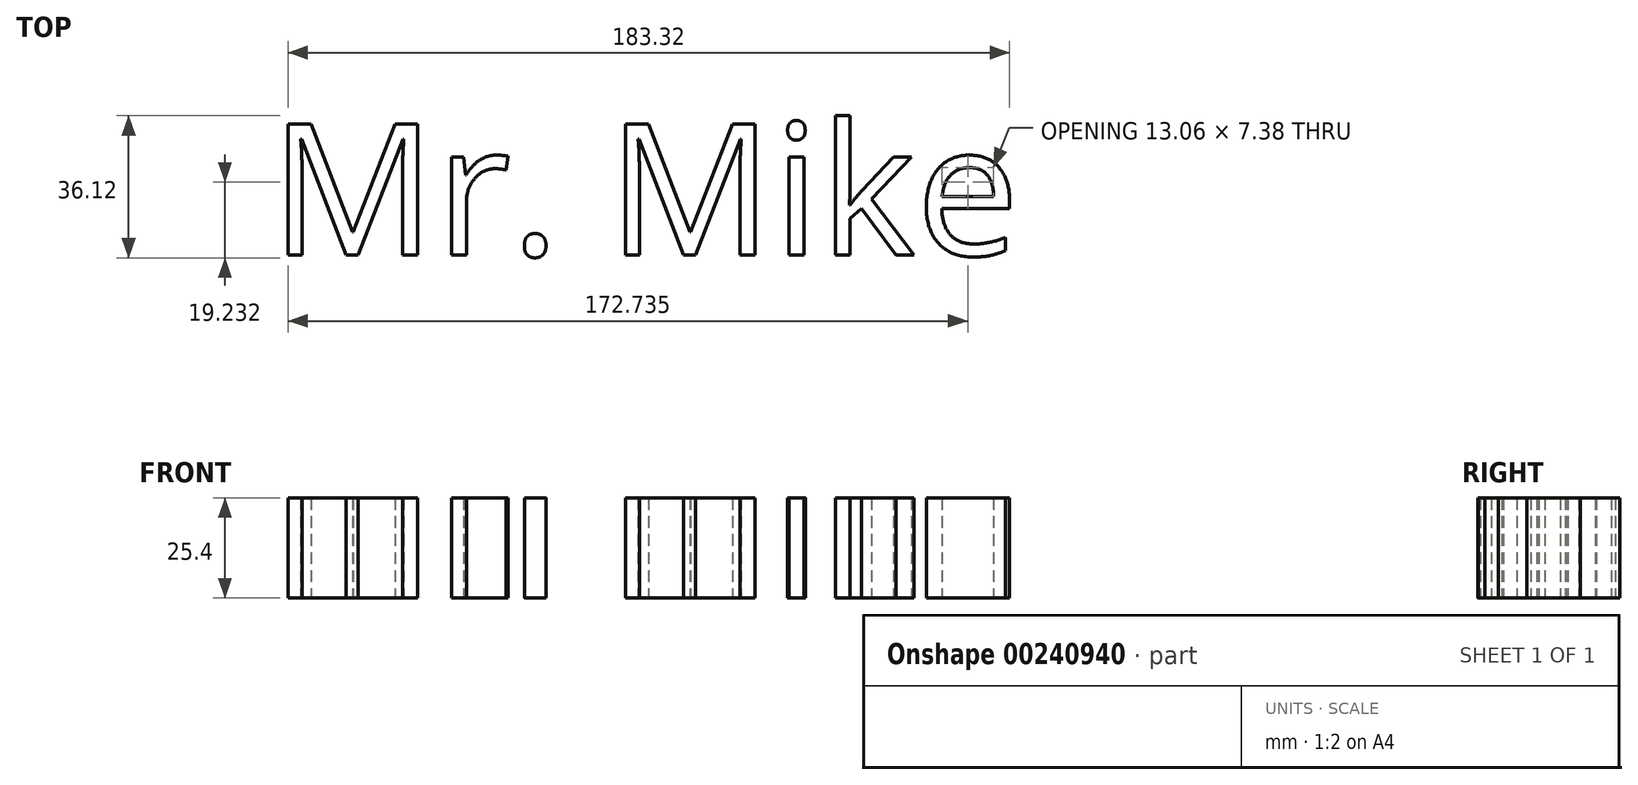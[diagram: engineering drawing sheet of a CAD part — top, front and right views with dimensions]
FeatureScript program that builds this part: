
annotation { "Feature Type Name" : "Feature", "Feature Type Description" : "" }
export const myFeature = defineFeature(function(context is Context, id is Id, definition is map)
    precondition{}
    {
        {
            var Q0;
            Q0=qCreatedBy(makeId("Top.planeOp"),FACE);
            var sketch = newSketch(context, id + "F0", { "sketchPlane" : qUnion([Q0])});
            skText(sketch, "E0", { "text": "Mr. Mike", "fontName": "OpenSans-Regular.ttf"});
            const initialGuessF0  = {"E0": [-0.15177, 6e-05, 1, 0, 0.0336]};
            skSetInitialGuess(sketch, initialGuessF0);
            skSolve(sketch);
        }
        {
            var Q0;
            Q0 = qSketchRegion(id + "F0", true);
            extrude(context, id + "F1", {"entities" : qUnion([Q0]), "depth" : 25.4 * mm});
        }
    });
